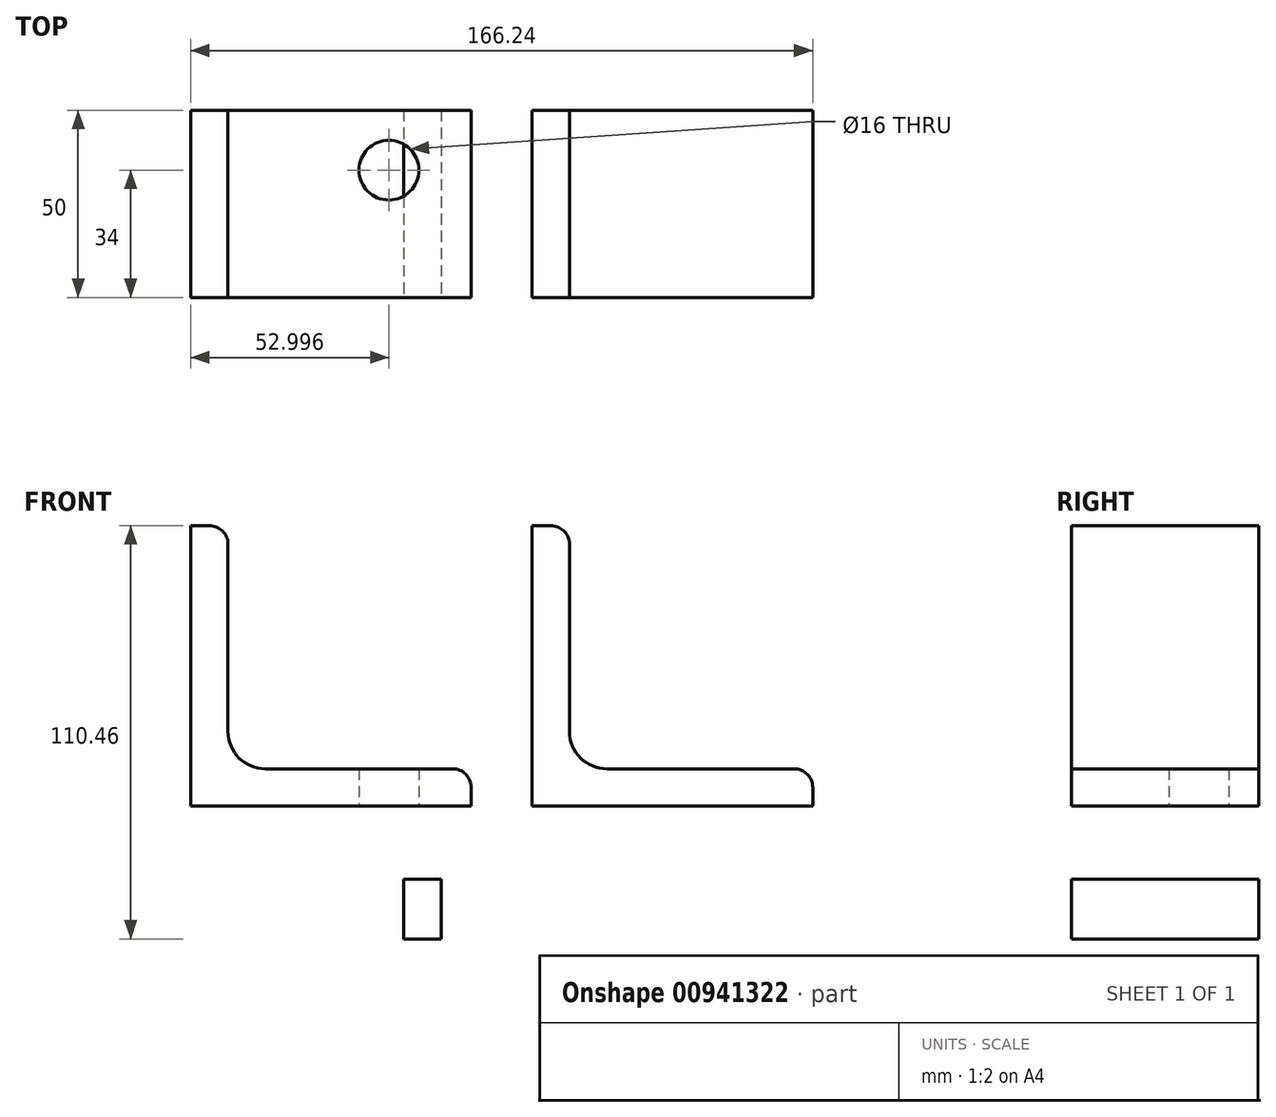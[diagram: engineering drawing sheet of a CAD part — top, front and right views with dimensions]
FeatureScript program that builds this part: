
annotation { "Feature Type Name" : "Feature", "Feature Type Description" : "" }
export const myFeature = defineFeature(function(context is Context, id is Id, definition is map)
    precondition{}
    {
        {
            var Q0;
            Q0=qCreatedBy(makeId("Front.planeOp"),FACE);
            var sketch = newSketch(context, id + "F0", { "sketchPlane" : qUnion([Q0])});
            skLineSegment(sketch, "E0", {"start": v(0, 0) * mm, "end": v(0, 75) * mm});
            skLineSegment(sketch, "E1", {"start": v(0, 75) * mm, "end": v(5, 75) * mm});
            skLineSegment(sketch, "E2", {"start": v(10, 70) * mm, "end": v(10, 20) * mm});
            skLineSegment(sketch, "E3", {"start": v(20, 10) * mm, "end": v(70, 10) * mm});
            skLineSegment(sketch, "E4", {"start": v(75, 5) * mm, "end": v(75, 0) * mm});
            skLineSegment(sketch, "E5", {"start": v(75, 0) * mm, "end": v(0, 0) * mm});
            skPoint(sketch, "E6.visualSharp", {"position": v(10, 10) * mm});
            skArc(sketch, "E6.filletArc", {"start": v(10, 20) * mm, "mid": v(12.93, 12.93) * mm, "end": v(20, 10) * mm});
            skPoint(sketch, "E7.visualSharp", {"position": v(10, 75) * mm});
            skArc(sketch, "E7.filletArc", {"start": v(10, 70) * mm, "mid": v(8.54, 73.54) * mm, "end": v(5, 75) * mm});
            skPoint(sketch, "E8.visualSharp", {"position": v(75, 10) * mm});
            skArc(sketch, "E8.filletArc", {"start": v(75, 5) * mm, "mid": v(73.54, 8.54) * mm, "end": v(70, 10) * mm});
            skSolve(sketch);
        }
        {
            var Q0;
            Q0=qCreatedBy(makeId("Front.planeOp"),FACE);
            var sketch = newSketch(context, id + "F1", { "sketchPlane" : qUnion([Q0])});
            skLineSegment(sketch, "E9", {"start": v(-91.24, 0) * mm, "end": v(-91.24, 75) * mm});
            skLineSegment(sketch, "E10", {"start": v(-91.24, 75) * mm, "end": v(-86.24, 75) * mm});
            skLineSegment(sketch, "E11", {"start": v(-81.24, 70) * mm, "end": v(-81.24, 20) * mm});
            skLineSegment(sketch, "E12", {"start": v(-71.24, 10) * mm, "end": v(-21.24, 10) * mm});
            skLineSegment(sketch, "E13", {"start": v(-16.24, 5) * mm, "end": v(-16.24, 0) * mm});
            skLineSegment(sketch, "E14", {"start": v(-16.24, 0) * mm, "end": v(-91.24, 0) * mm});
            skPoint(sketch, "E15.visualSharp", {"position": v(-81.24, 10) * mm});
            skArc(sketch, "E15.filletArc", {"start": v(-81.24, 20) * mm, "mid": v(-78.32, 12.93) * mm, "end": v(-71.24, 10) * mm});
            skPoint(sketch, "E16.visualSharp", {"position": v(-81.24, 75) * mm});
            skArc(sketch, "E16.filletArc", {"start": v(-81.24, 70) * mm, "mid": v(-82.7, 73.54) * mm, "end": v(-86.24, 75) * mm});
            skPoint(sketch, "E17.visualSharp", {"position": v(-16.24, 10) * mm});
            skArc(sketch, "E17.filletArc", {"start": v(-16.24, 5) * mm, "mid": v(-17.7, 8.54) * mm, "end": v(-21.24, 10) * mm});
            skSolve(sketch);
        }
        {
            var Q0;
            Q0 = qSketchRegion(id + "F0", true);
            var Q1;
            Q1 = qSketchRegion(id + "F1", true);
            extrude(context, id + "F2", {"entities" : qUnion([Q0, Q1]), "oppositeDirection" : true, "depth" : 50 * mm, "offsetDistance" : 25 * mm});
        }
        {
            var Q0;
            Q0=makeQuery(id+"F2.opExtrude","SWEPT_FACE",FACE,{"disambiguationData":[OSD([sQuery(id+"F1.wireOp",EDGE,"E14")])]});
            var sketch = newSketch(context, id + "F3", { "sketchPlane" : qUnion([Q0])});
            skCircle(sketch, "E18", {"center": v(-38.24, -34) * mm, "radius": 8 * mm});
            skPoint(sketch, "E18.centerSnap0", {"position": v(-16.24, -34) * mm});
            skSolve(sketch);
        }
        {
            var Q0;
            Q0 = qSketchRegion(id + "F3", true);
            var Q1;
            Q1=makeQuery(id+"F2.opExtrude","SWEPT_FACE",FACE,{"disambiguationData":[OSD([sQuery(id+"F1.wireOp",EDGE,"E12")])]});
            extrude(context, id + "F4", {"entities" : qUnion([Q0]), "operationType" : NewBodyOperationType.REMOVE, "endBound" : BoundingType.UP_TO_SURFACE, "oppositeDirection" : true, "depth" : 25 * mm, "endBoundEntityFace" : qUnion([Q1]), "offsetDistance" : 25 * mm});
        }
        {
            var Q0;
            Q0=qCreatedBy(makeId("Front.planeOp"),FACE);
            var sketch = newSketch(context, id + "F5", { "sketchPlane" : qUnion([Q0])});
            skLineSegment(sketch, "E19.bottom", {"start": v(-34.3, -35.46) * mm, "end": v(-24.3, -35.46) * mm});
            skLineSegment(sketch, "E19.top", {"start": v(-34.3, -19.46) * mm, "end": v(-24.3, -19.46) * mm});
            skLineSegment(sketch, "E19.left", {"start": v(-34.3, -35.46) * mm, "end": v(-34.3, -19.46) * mm});
            skLineSegment(sketch, "E19.right", {"start": v(-24.3, -35.46) * mm, "end": v(-24.3, -19.46) * mm});
            skSolve(sketch);
        }
        {
            var Q0;
            Q0 = qSketchRegion(id + "F5", true);
            extrude(context, id + "F6", {"entities" : qUnion([Q0]), "oppositeDirection" : true, "depth" : 50 * mm, "offsetDistance" : 25 * mm});
        }
    });
